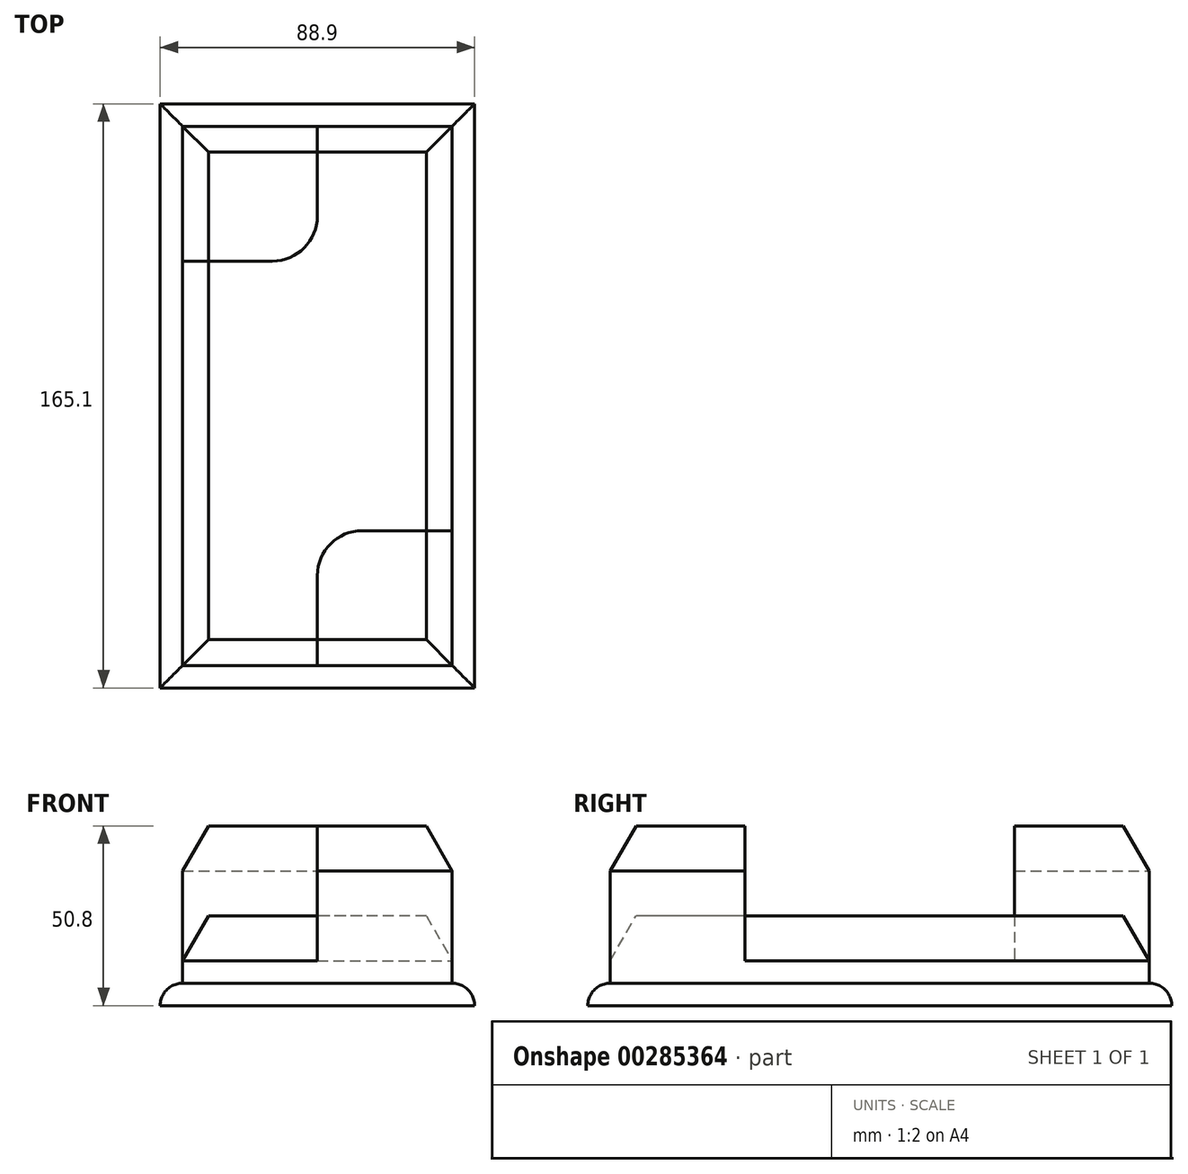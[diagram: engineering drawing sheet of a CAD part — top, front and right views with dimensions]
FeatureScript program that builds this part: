
annotation { "Feature Type Name" : "Feature", "Feature Type Description" : "" }
export const myFeature = defineFeature(function(context is Context, id is Id, definition is map)
    precondition{}
    {
        {
            var Q0;
            Q0=qCreatedBy(makeId("Top.planeOp"),FACE);
            var sketch = newSketch(context, id + "F0", { "sketchPlane" : qUnion([Q0])});
            skLineSegment(sketch, "E0", {"start": v(-59.94, 83.3) * mm, "end": v(28.96, 83.3) * mm});
            skLineSegment(sketch, "E1", {"start": v(28.96, 83.3) * mm, "end": v(28.96, -81.8) * mm});
            skLineSegment(sketch, "E2", {"start": v(28.96, -81.8) * mm, "end": v(-59.94, -81.8) * mm});
            skLineSegment(sketch, "E3", {"start": v(-59.94, -81.8) * mm, "end": v(-59.94, 83.3) * mm});
            skLineSegment(sketch, "E4", {"start": v(-53.6, 76.95) * mm, "end": v(22.6, 76.95) * mm});
            skLineSegment(sketch, "E5", {"start": v(22.6, 76.95) * mm, "end": v(22.6, -75.45) * mm});
            skLineSegment(sketch, "E6", {"start": v(22.6, -75.45) * mm, "end": v(-53.6, -75.45) * mm});
            skLineSegment(sketch, "E7", {"start": v(-53.6, -75.45) * mm, "end": v(-53.6, 76.95) * mm});
            skLineSegment(sketch, "E8", {"start": v(-15.5, 76.95) * mm, "end": v(-15.5, 51.55) * mm});
            skLineSegment(sketch, "E9", {"start": v(-28.2, 38.85) * mm, "end": v(-53.6, 38.85) * mm});
            skLineSegment(sketch, "E10", {"start": v(22.6, -37.35) * mm, "end": v(-2.8, -37.35) * mm});
            skLineSegment(sketch, "E11", {"start": v(-15.5, -50.05) * mm, "end": v(-15.5, -75.45) * mm});
            skPoint(sketch, "E12.visualSharp", {"position": v(-15.5, 38.85) * mm});
            skArc(sketch, "E12.filletArc", {"start": v(-28.2, 38.85) * mm, "mid": v(-19.21, 42.57) * mm, "end": v(-15.5, 51.55) * mm});
            skPoint(sketch, "E13.visualSharp", {"position": v(-15.5, -37.35) * mm});
            skArc(sketch, "E13.filletArc", {"start": v(-2.8, -37.35) * mm, "mid": v(-11.77, -41.07) * mm, "end": v(-15.5, -50.05) * mm});
            skSolve(sketch);
        }
        {
            var Q0;
            Q0=makeQuery(id+"F0.imprint","IMPRINT",FACE,{"disambiguationData":[TD([[makeQuery(id+"F0.imprint","IMPRINT",EDGE,{"derivedFrom":sQuery(id+"F0.wireOp",EDGE,"E0")}),-1.0]])]});
            extrude(context, id + "F1", {"entities" : qUnion([Q0]), "depth" : 6.35 * mm});
        }
        {
            var Q0;
            {var subQ9=sQuery(id+"F0.wireOp",EDGE,"E8");Q0=makeQuery(id+"F0.imprint","IMPRINT",FACE,{"disambiguationData":[TD([[makeQuery(id+"F0.imprint","IMPRINT",EDGE,{"derivedFrom":subQ9}),1.0]])]});}
            extrude(context, id + "F2", {"entities" : qUnion([Q0]), "operationType" : NewBodyOperationType.ADD, "depth" : 25.4 * mm});
        }
        {
            var Q0;
            {var subQ1=sQuery(id+"F0.wireOp",EDGE,"E8");Q0=makeQuery(id+"F0.imprint","IMPRINT",FACE,{"disambiguationData":[TD([[makeQuery(id+"F0.imprint","IMPRINT",EDGE,{"derivedFrom":subQ1}),-1.0]])]});}
            var Q1;
            {var subQ1=sQuery(id+"F0.wireOp",EDGE,"E10");Q1=makeQuery(id+"F0.imprint","IMPRINT",FACE,{"disambiguationData":[TD([[makeQuery(id+"F0.imprint","IMPRINT",EDGE,{"derivedFrom":subQ1}),1.0]])]});}
            extrude(context, id + "F3", {"entities" : qUnion([Q0, Q1]), "operationType" : NewBodyOperationType.ADD, "depth" : 50.8 * mm});
        }
        {
            var Q0;
            Q0=makeQuery(id+"F1.opExtrude","CAP_EDGE",EDGE,{"disambiguationData":[OSD([sQuery(id+"F0.wireOp",EDGE,"E1")])],"isStart":false});
            var Q1;
            Q1=makeQuery(id+"F1.opExtrude","CAP_EDGE",EDGE,{"disambiguationData":[OSD([sQuery(id+"F0.wireOp",EDGE,"E2")])],"isStart":false});
            var Q2;
            Q2=makeQuery(id+"F1.opExtrude","CAP_EDGE",EDGE,{"disambiguationData":[OSD([sQuery(id+"F0.wireOp",EDGE,"E3")])],"isStart":false});
            var Q3;
            Q3=makeQuery(id+"F1.opExtrude","CAP_EDGE",EDGE,{"disambiguationData":[OSD([sQuery(id+"F0.wireOp",EDGE,"E0")])],"isStart":false});
            fillet(context, id + "F4", {"entities" : qUnion([Q0, Q1, Q2, Q3]), "radius" : 6.35 * mm, "tangentPropagation" : true, "allowEdgeOverflow" : false});
        }
        {
            var Q0;
            Q0=makeQuery(id+"F2.opExtrude","CAP_EDGE",EDGE,{"disambiguationData":[OSD([sQuery(id+"F0.wireOp",EDGE,"E6")])],"isStart":false});
            var Q1;
            Q1=makeQuery(id+"F2.opExtrude","CAP_EDGE",EDGE,{"disambiguationData":[OSD([sQuery(id+"F0.wireOp",EDGE,"E7")])],"isStart":false});
            var Q2;
            Q2=makeQuery(id+"F2.opExtrude","CAP_EDGE",EDGE,{"disambiguationData":[OSD([sQuery(id+"F0.wireOp",EDGE,"E5")])],"isStart":false});
            var Q3;
            Q3=makeQuery(id+"F2.opExtrude","CAP_EDGE",EDGE,{"disambiguationData":[OSD([sQuery(id+"F0.wireOp",EDGE,"E4")])],"isStart":false});
            chamfer(context, id + "F5", {"entities" : qUnion([Q0, Q1, Q2, Q3]), "chamferType" : ChamferType.OFFSET_ANGLE, "width" : 12.7 * mm, "oppositeDirection" : false, "angle" : 30 * degree, "tangentPropagation" : true});
        }
        {
            var Q0;
            Q0=makeQuery(id+"F3.opExtrude","CAP_EDGE",EDGE,{"disambiguationData":[OSD([sQuery(id+"F0.wireOp",EDGE,"E5")])],"isStart":false});
            var Q1;
            Q1=makeQuery(id+"F3.opExtrude","CAP_EDGE",EDGE,{"disambiguationData":[OSD([sQuery(id+"F0.wireOp",EDGE,"E6")])],"isStart":false});
            var Q2;
            Q2=makeQuery(id+"F3.opExtrude","CAP_EDGE",EDGE,{"disambiguationData":[OSD([sQuery(id+"F0.wireOp",EDGE,"E4")])],"isStart":false});
            var Q3;
            Q3=makeQuery(id+"F3.opExtrude","CAP_EDGE",EDGE,{"disambiguationData":[OSD([sQuery(id+"F0.wireOp",EDGE,"E7")])],"isStart":false});
            chamfer(context, id + "F6", {"entities" : qUnion([Q0, Q1, Q2, Q3]), "chamferType" : ChamferType.OFFSET_ANGLE, "width" : 12.7 * mm, "oppositeDirection" : false, "angle" : 30 * degree, "tangentPropagation" : true});
        }
    });
